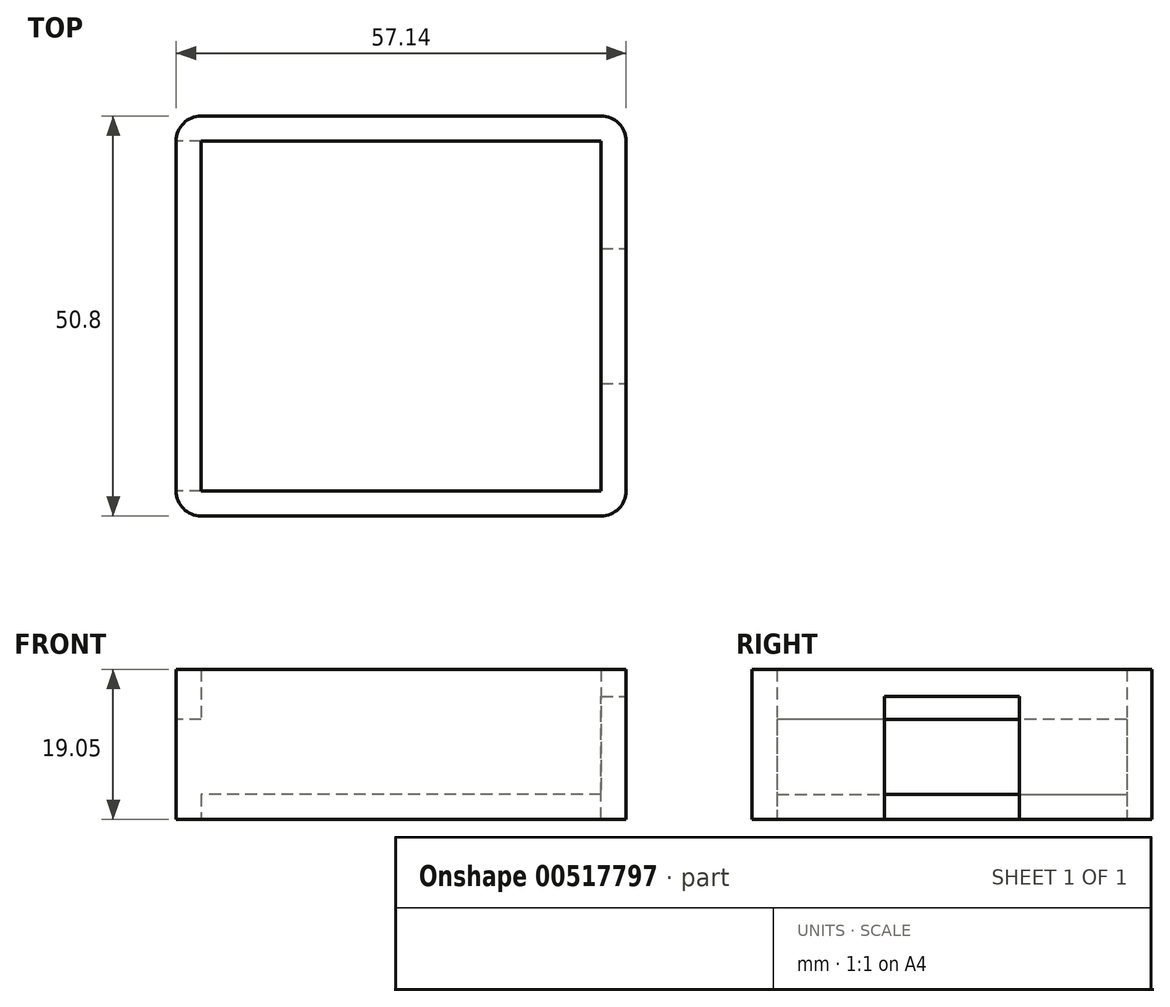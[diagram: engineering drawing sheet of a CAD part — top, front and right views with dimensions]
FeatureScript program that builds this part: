
annotation { "Feature Type Name" : "Feature", "Feature Type Description" : "" }
export const myFeature = defineFeature(function(context is Context, id is Id, definition is map)
    precondition{}
    {
        {
            var Q0;
            Q0=qCreatedBy(makeId("Top.planeOp"),FACE);
            var sketch = newSketch(context, id + "F0", { "sketchPlane" : qUnion([Q0])});
            skLineSegment(sketch, "E0.bottom", {"start": v(25.4, -25.4) * mm, "end": v(-25.4, -25.4) * mm});
            skLineSegment(sketch, "E0.top", {"start": v(25.4, 25.4) * mm, "end": v(-25.4, 25.4) * mm});
            skLineSegment(sketch, "E0.left", {"start": v(28.58, -22.23) * mm, "end": v(28.58, 22.23) * mm});
            skLineSegment(sketch, "E0.right", {"start": v(-28.57, -22.23) * mm, "end": v(-28.57, 22.22) * mm});
            skPoint(sketch, "E0.middle", {"position": v(0, 0) * mm});
            skPoint(sketch, "E1.visualSharp", {"position": v(28.58, 25.4) * mm});
            skArc(sketch, "E1.filletArc", {"start": v(28.58, 22.23) * mm, "mid": v(27.65, 24.47) * mm, "end": v(25.4, 25.4) * mm});
            skPoint(sketch, "E2.visualSharp", {"position": v(28.58, -25.4) * mm});
            skArc(sketch, "E2.filletArc", {"start": v(25.4, -25.4) * mm, "mid": v(27.65, -24.47) * mm, "end": v(28.58, -22.23) * mm});
            skPoint(sketch, "E3.visualSharp", {"position": v(-28.57, -25.4) * mm});
            skArc(sketch, "E3.filletArc", {"start": v(-28.58, -22.23) * mm, "mid": v(-27.65, -24.47) * mm, "end": v(-25.4, -25.4) * mm});
            skPoint(sketch, "E4.visualSharp", {"position": v(-28.57, 25.4) * mm});
            skArc(sketch, "E4.filletArc", {"start": v(-25.4, 25.4) * mm, "mid": v(-27.65, 24.47) * mm, "end": v(-28.58, 22.22) * mm});
            skSolve(sketch);
        }
        {
            var Q0;
            Q0 = qSketchRegion(id + "F0", true);
            extrude(context, id + "F1", {"entities" : qUnion([Q0]), "depth" : 19.05 * mm, "offsetDistance" : 25.4 * mm});
        }
        {
            var Q0;
            Q0=makeQuery(id+"F1.opExtrude","CAP_FACE",FACE,{"disambiguationData":[OSD([sQuery(id+"F0.wireOp",EDGE,"E0.bottom"),sQuery(id+"F0.wireOp",EDGE,"E0.top"),sQuery(id+"F0.wireOp",EDGE,"E0.left"),sQuery(id+"F0.wireOp",EDGE,"E0.right"),sQuery(id+"F0.wireOp",EDGE,"E1.filletArc"),sQuery(id+"F0.wireOp",EDGE,"E2.filletArc"),sQuery(id+"F0.wireOp",EDGE,"E4.filletArc"),sQuery(id+"F0.wireOp",EDGE,"E3.filletArc")])],"isStart":false});
            shell(context, id + "F2", {"entities" : qUnion([Q0]), "thickness" : 3.17 * mm});
        }
        {
            var Q0;
            Q0=makeQuery(id+"F1.opExtrude","SWEPT_FACE",FACE,{"disambiguationData":[OSD([sQuery(id+"F0.wireOp",EDGE,"E0.left")])]});
            var sketch = newSketch(context, id + "F3", { "sketchPlane" : qUnion([Q0])});
            skLineSegment(sketch, "E5.bottom", {"start": v(8.57, 0) * mm, "end": v(-8.57, 0) * mm});
            skLineSegment(sketch, "E5.top", {"start": v(8.57, 15.62) * mm, "end": v(-8.57, 15.62) * mm});
            skLineSegment(sketch, "E5.left", {"start": v(8.57, 0) * mm, "end": v(8.57, 15.62) * mm});
            skLineSegment(sketch, "E5.right", {"start": v(-8.57, 0) * mm, "end": v(-8.57, 15.62) * mm});
            skPoint(sketch, "E5.middle", {"position": v(0, 7.81) * mm});
            skPoint(sketch, "E5.middle.positionSnap0", {"position": v(0, 0) * mm});
            skPoint(sketch, "E5.centerSnap0", {"position": v(0, 0) * mm});
            skSolve(sketch);
        }
        {
            var Q0;
            Q0=makeQuery(id+"F3.imprint","IMPRINT",FACE,{"disambiguationData":[TD([[makeQuery(id+"F3.imprint","IMPRINT",EDGE,{"derivedFrom":sQuery(id+"F3.wireOp",EDGE,"E5.bottom")}),1.0]])]});
            extrude(context, id + "F4", {"entities" : qUnion([Q0]), "operationType" : NewBodyOperationType.REMOVE, "oppositeDirection" : true, "depth" : 3.17 * mm, "offsetDistance" : 25.4 * mm});
        }
        {
            var Q0;
            Q0=makeQuery(id+"F1.opExtrude","SWEPT_FACE",FACE,{"disambiguationData":[OSD([sQuery(id+"F0.wireOp",EDGE,"E0.right")])]});
            var sketch = newSketch(context, id + "F5", { "sketchPlane" : qUnion([Q0])});
            skLineSegment(sketch, "E6.bottom", {"start": v(-22.22, 0) * mm, "end": v(22.23, 0) * mm});
            skLineSegment(sketch, "E6.top", {"start": v(-22.22, 12.7) * mm, "end": v(22.23, 12.7) * mm});
            skLineSegment(sketch, "E6.left", {"start": v(-22.22, 0) * mm, "end": v(-22.22, 12.7) * mm});
            skLineSegment(sketch, "E6.right", {"start": v(22.23, 0) * mm, "end": v(22.23, 12.7) * mm});
            skSolve(sketch);
        }
        {
            var Q0;
            Q0=makeQuery(id+"F5.imprint","IMPRINT",FACE,{"disambiguationData":[TD([[makeQuery(id+"F5.imprint","IMPRINT",EDGE,{"derivedFrom":sQuery(id+"F5.wireOp",EDGE,"E6.bottom")}),-1.0]])]});
            extrude(context, id + "F6", {"entities" : qUnion([Q0]), "operationType" : NewBodyOperationType.REMOVE, "oppositeDirection" : true, "depth" : 3.17 * mm, "offsetDistance" : 25.4 * mm});
        }
    });
